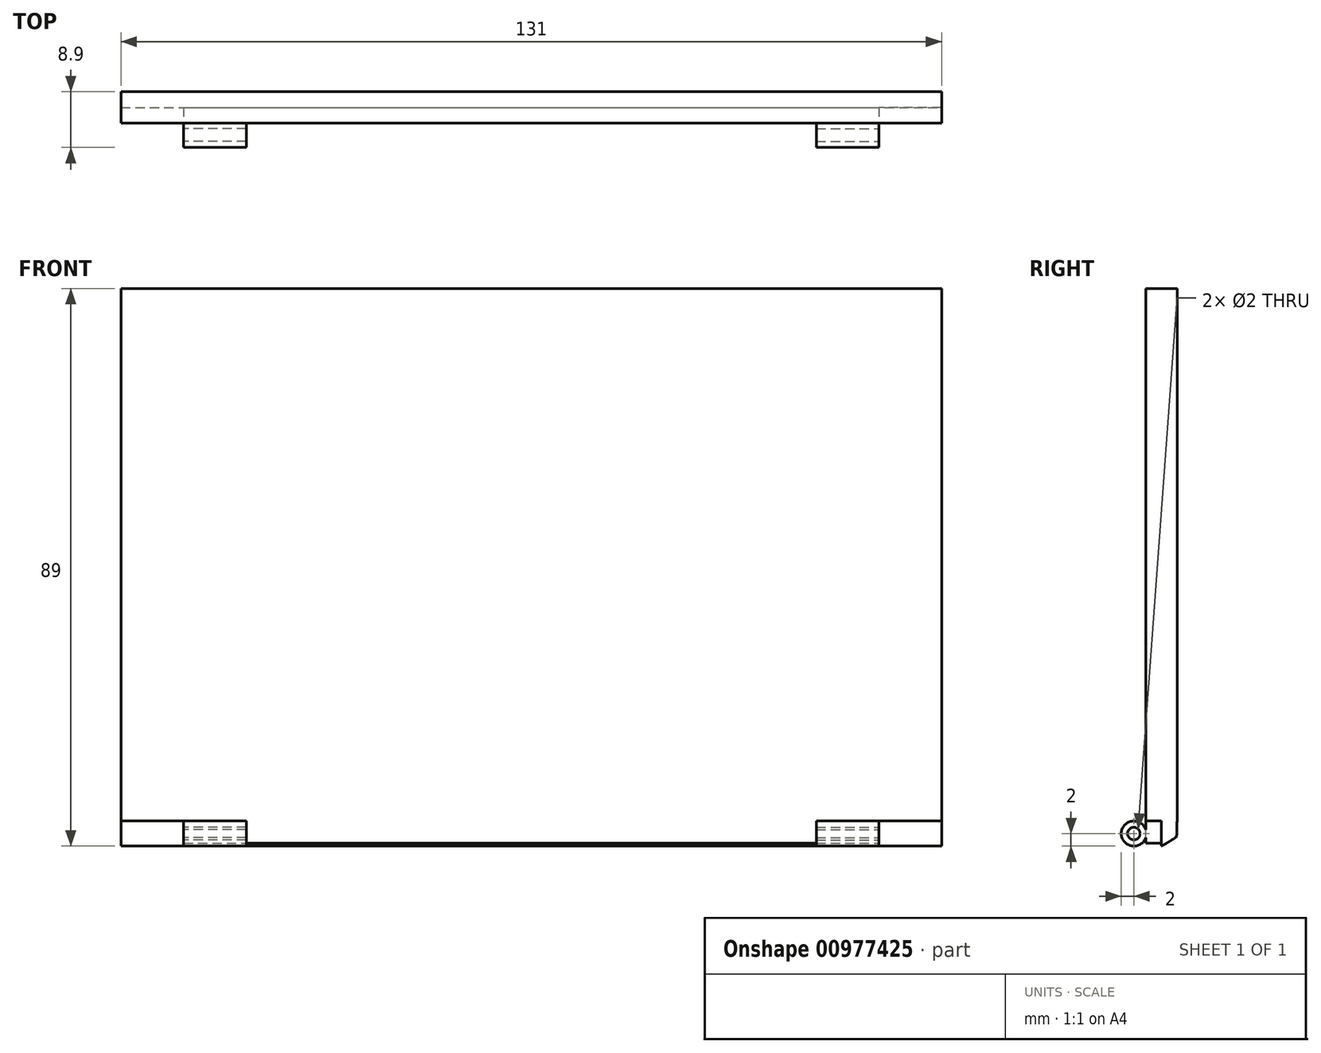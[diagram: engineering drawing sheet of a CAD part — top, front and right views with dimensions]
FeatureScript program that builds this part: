
annotation { "Feature Type Name" : "Feature", "Feature Type Description" : "" }
export const myFeature = defineFeature(function(context is Context, id is Id, definition is map)
    precondition{}
    {
        {
            var Q0;
            Q0=qCreatedBy(makeId("Front.planeOp"),FACE);
            var sketch = newSketch(context, id + "F0", { "sketchPlane" : qUnion([Q0])});
            skLineSegment(sketch, "E0.bottom", {"start": v(-65.5, 44.5) * mm, "end": v(65.5, 44.5) * mm});
            skLineSegment(sketch, "E0.top", {"start": v(-65.5, -44.5) * mm, "end": v(65.5, -44.5) * mm});
            skLineSegment(sketch, "E0.left", {"start": v(-65.5, 44.5) * mm, "end": v(-65.5, -44.5) * mm});
            skLineSegment(sketch, "E0.right", {"start": v(65.5, 44.5) * mm, "end": v(65.5, -44.5) * mm});
            skPoint(sketch, "E0.middle", {"position": v(0, 0) * mm});
            skSolve(sketch);
        }
        {
            var Q0;
            Q0=qSketchRegion(id+"F0",true);
            extrude(context, id + "F1", {"entities" : qUnion([Q0]), "depth" : 5 * mm, "offsetDistance" : 25 * mm});
        }
        {
            var Q0;
            Q0=makeQuery(id+"F1.opExtrude","SWEPT_FACE",FACE,{"disambiguationData":[OSD([sQuery(id+"F0.wireOp",EDGE,"E0.left")])]});
            var sketch = newSketch(context, id + "F2", { "sketchPlane" : qUnion([Q0])});
            skCircle(sketch, "E1", {"center": v(6.9, -42.5) * mm, "radius": 2 * mm});
            skCircle(sketch, "E2", {"center": v(6.9, -42.5) * mm, "radius": 1 * mm});
            skSolve(sketch);
        }
        {
            var Q0;
            Q0=qSketchRegion(id+"F2",true);
            extrude(context, id + "F3", {"entities" : qUnion([Q0]), "operationType" : NewBodyOperationType.ADD, "oppositeDirection" : true, "depth" : 20 * mm, "offsetDistance" : 25 * mm, "hasSecondDirection" : true, "secondDirectionOppositeDirection" : true, "secondDirectionDepth" : 10 * mm});
        }
        {
            var Q0;
            Q0=makeQuery(id+"F1.opExtrude","SWEPT_FACE",FACE,{"disambiguationData":[OSD([sQuery(id+"F0.wireOp",EDGE,"E0.right")])]});
            var sketch = newSketch(context, id + "F4", { "sketchPlane" : qUnion([Q0])});
            skCircle(sketch, "E3", {"center": v(-6.9, -42.5) * mm, "radius": 2 * mm});
            skCircle(sketch, "E4", {"center": v(-6.9, -42.5) * mm, "radius": 1 * mm});
            skSolve(sketch);
        }
        {
            var Q0;
            Q0=qSketchRegion(id+"F4",true);
            extrude(context, id + "F5", {"entities" : qUnion([Q0]), "operationType" : NewBodyOperationType.ADD, "oppositeDirection" : true, "depth" : 20 * mm, "offsetDistance" : 25 * mm, "hasSecondDirection" : true, "secondDirectionOppositeDirection" : true, "secondDirectionDepth" : 10 * mm});
        }
        {
            var Q0;
            Q0=makeQuery(id+"F1.opExtrude","CAP_FACE",FACE,{"disambiguationData":[OSD([sQuery(id+"F0.wireOp",EDGE,"E0.bottom"),sQuery(id+"F0.wireOp",EDGE,"E0.top"),sQuery(id+"F0.wireOp",EDGE,"E0.left"),sQuery(id+"F0.wireOp",EDGE,"E0.right")])],"isStart":false});
            var sketch = newSketch(context, id + "F6", { "sketchPlane" : qUnion([Q0])});
            skLineSegment(sketch, "E5.bottom", {"start": v(65.5, -44.5) * mm, "end": v(55.5, -44.5) * mm});
            skLineSegment(sketch, "E5.top", {"start": v(65.5, -40.5) * mm, "end": v(55.5, -40.5) * mm});
            skLineSegment(sketch, "E5.left", {"start": v(65.5, -44.5) * mm, "end": v(65.5, -40.5) * mm});
            skLineSegment(sketch, "E5.right", {"start": v(55.5, -44.5) * mm, "end": v(55.5, -40.5) * mm});
            skLineSegment(sketch, "E6.bottom", {"start": v(-65.5, -44.5) * mm, "end": v(-55.5, -44.5) * mm});
            skLineSegment(sketch, "E6.top", {"start": v(-65.5, -40.5) * mm, "end": v(-55.5, -40.5) * mm});
            skLineSegment(sketch, "E6.left", {"start": v(-65.5, -44.5) * mm, "end": v(-65.5, -40.5) * mm});
            skLineSegment(sketch, "E6.right", {"start": v(-55.5, -44.5) * mm, "end": v(-55.5, -40.5) * mm});
            skLineSegment(sketch, "E7.right", {"start": v(55.5, -44.5) * mm, "end": v(55.5, -44.5) * mm});
            skLineSegment(sketch, "E8.bottom", {"start": v(-55.5, -44.5) * mm, "end": v(55.5, -44.5) * mm});
            skLineSegment(sketch, "E8.top", {"start": v(-55.5, -44) * mm, "end": v(55.5, -44) * mm});
            skLineSegment(sketch, "E8.left", {"start": v(-55.5, -44.5) * mm, "end": v(-55.5, -44) * mm});
            skLineSegment(sketch, "E8.right", {"start": v(55.5, -44.5) * mm, "end": v(55.5, -44) * mm});
            skSolve(sketch);
        }
        {
            var Q0;
            Q0=qSketchRegion(id+"F6",true);
            extrude(context, id + "F7", {"entities" : qUnion([Q0]), "operationType" : NewBodyOperationType.REMOVE, "oppositeDirection" : true, "depth" : 2.5 * mm, "offsetDistance" : 25 * mm});
        }
        {
            var Q0;
            Q0=makeQuery(id+"F1.opExtrude","CAP_EDGE",EDGE,{"disambiguationData":[OSD([sQuery(id+"F0.wireOp",EDGE,"E0.top")])],"isStart":true});
            fillet(context, id + "F8", {"entities" : qUnion([Q0]), "radius" : 5 * mm, "tangentPropagation" : true, "rho" : 0.9, "crossSection" : FilletCrossSection.CONIC, "allowEdgeOverflow" : false});
        }
    });
